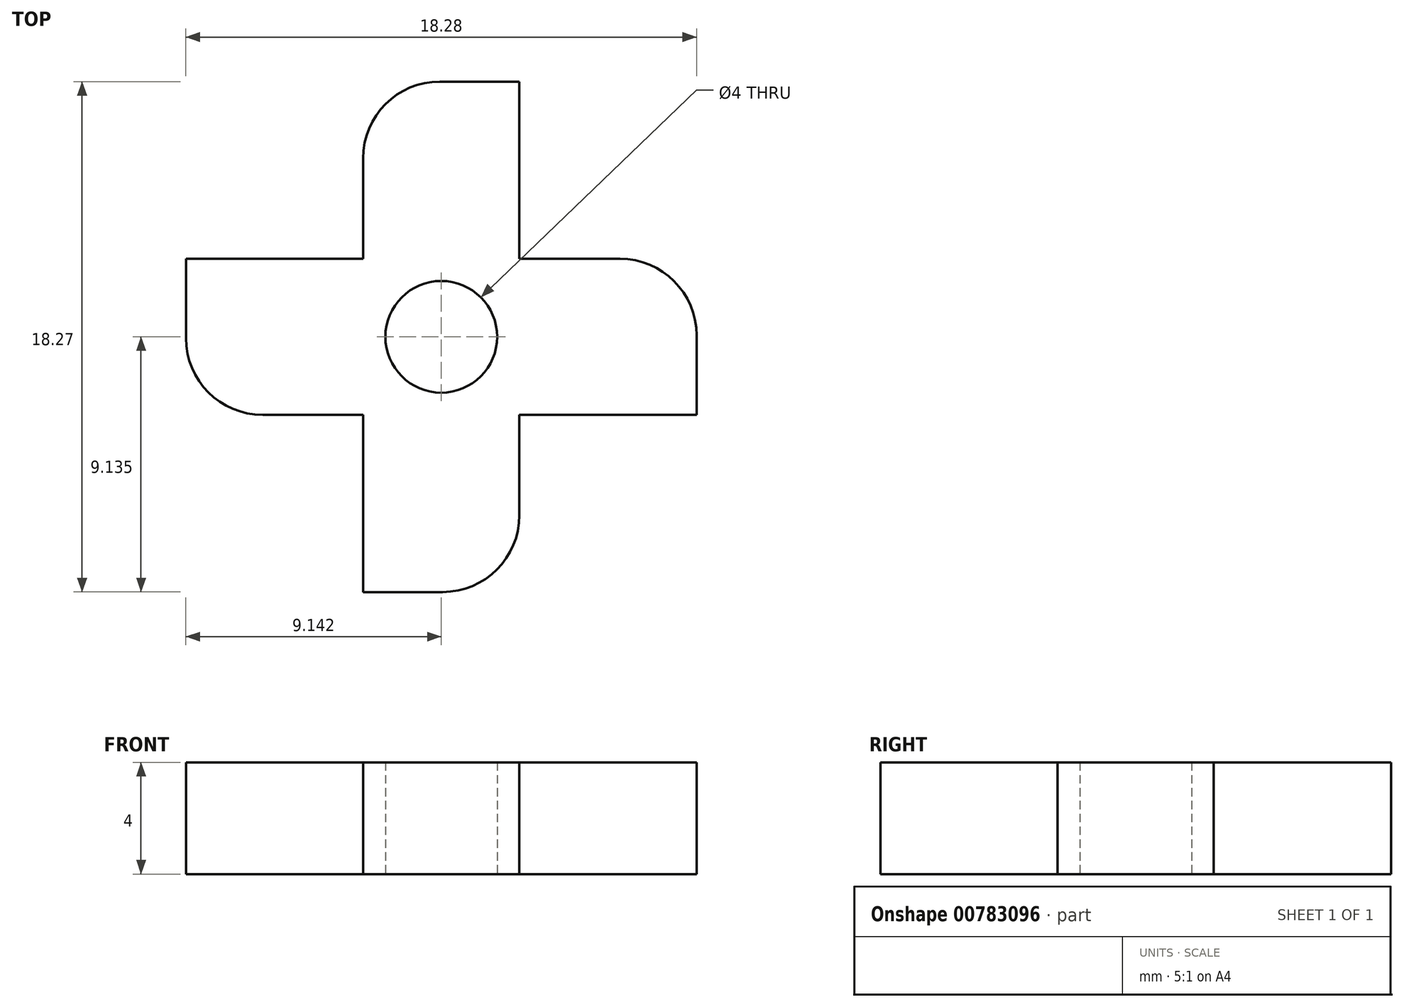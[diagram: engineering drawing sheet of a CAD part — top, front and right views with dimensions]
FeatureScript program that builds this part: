
annotation { "Feature Type Name" : "Feature", "Feature Type Description" : "" }
export const myFeature = defineFeature(function(context is Context, id is Id, definition is map)
    precondition{}
    {
        {
            var Q0;
            Q0=qCreatedBy(makeId("Top.planeOp"),FACE);
            var sketch = newSketch(context, id + "F0", { "sketchPlane" : qUnion([Q0])});
            skLineSegment(sketch, "E0.bottom", {"start": v(-58.09, 30.47) * mm, "end": v(-42.56, 30.47) * mm});
            skLineSegment(sketch, "E0.top", {"start": v(-55.34, 24.88) * mm, "end": v(-39.81, 24.88) * mm});
            skLineSegment(sketch, "E0.left", {"start": v(-39.81, 27.73) * mm, "end": v(-39.81, 24.88) * mm});
            skLineSegment(sketch, "E0.right", {"start": v(-58.09, 30.47) * mm, "end": v(-58.09, 27.62) * mm});
            skLineSegment(sketch, "E1.bottom", {"start": v(-51.74, 18.54) * mm, "end": v(-51.74, 34.07) * mm});
            skLineSegment(sketch, "E1.top", {"start": v(-46.15, 21.28) * mm, "end": v(-46.15, 36.81) * mm});
            skLineSegment(sketch, "E1.left", {"start": v(-51.74, 18.54) * mm, "end": v(-48.9, 18.54) * mm});
            skLineSegment(sketch, "E1.right", {"start": v(-49, 36.81) * mm, "end": v(-46.15, 36.81) * mm});
            skPoint(sketch, "E2", {"position": v(-48.95, 27.67) * mm});
            skPoint(sketch, "E2.positionSnap0", {"position": v(-48.95, 30.47) * mm});
            skPoint(sketch, "E2.positionSnap1", {"position": v(-39.81, 27.67) * mm});
            skPoint(sketch, "E3.positionSnap0", {"position": v(-46.15, 27.67) * mm});
            skPoint(sketch, "E3.positionSnap1", {"position": v(-48.95, 18.54) * mm});
            skPoint(sketch, "E4.visualSharp", {"position": v(-51.74, 36.81) * mm});
            skArc(sketch, "E4.filletArc", {"start": v(-49, 36.81) * mm, "mid": v(-50.94, 36) * mm, "end": v(-51.74, 34.07) * mm});
            skPoint(sketch, "E5.visualSharp", {"position": v(-46.15, 18.54) * mm});
            skArc(sketch, "E5.filletArc", {"start": v(-48.9, 18.54) * mm, "mid": v(-46.96, 19.34) * mm, "end": v(-46.15, 21.28) * mm});
            skPoint(sketch, "E6.visualSharp", {"position": v(-39.81, 30.47) * mm});
            skArc(sketch, "E6.filletArc", {"start": v(-39.81, 27.73) * mm, "mid": v(-40.61, 29.67) * mm, "end": v(-42.56, 30.47) * mm});
            skPoint(sketch, "E7.visualSharp", {"position": v(-58.09, 24.88) * mm});
            skArc(sketch, "E7.filletArc", {"start": v(-58.09, 27.62) * mm, "mid": v(-57.28, 25.68) * mm, "end": v(-55.34, 24.88) * mm});
            skCircle(sketch, "E8", {"center": v(-48.95, 27.67) * mm, "radius": 2 * mm});
            skSolve(sketch);
        }
        {
            var Q0;
            Q0 = qSketchRegion(id + "F0", true);
            extrude(context, id + "F1", {"entities" : qUnion([Q0]), "depth" : 4 * mm, "offsetDistance" : 25 * mm});
        }
    });
